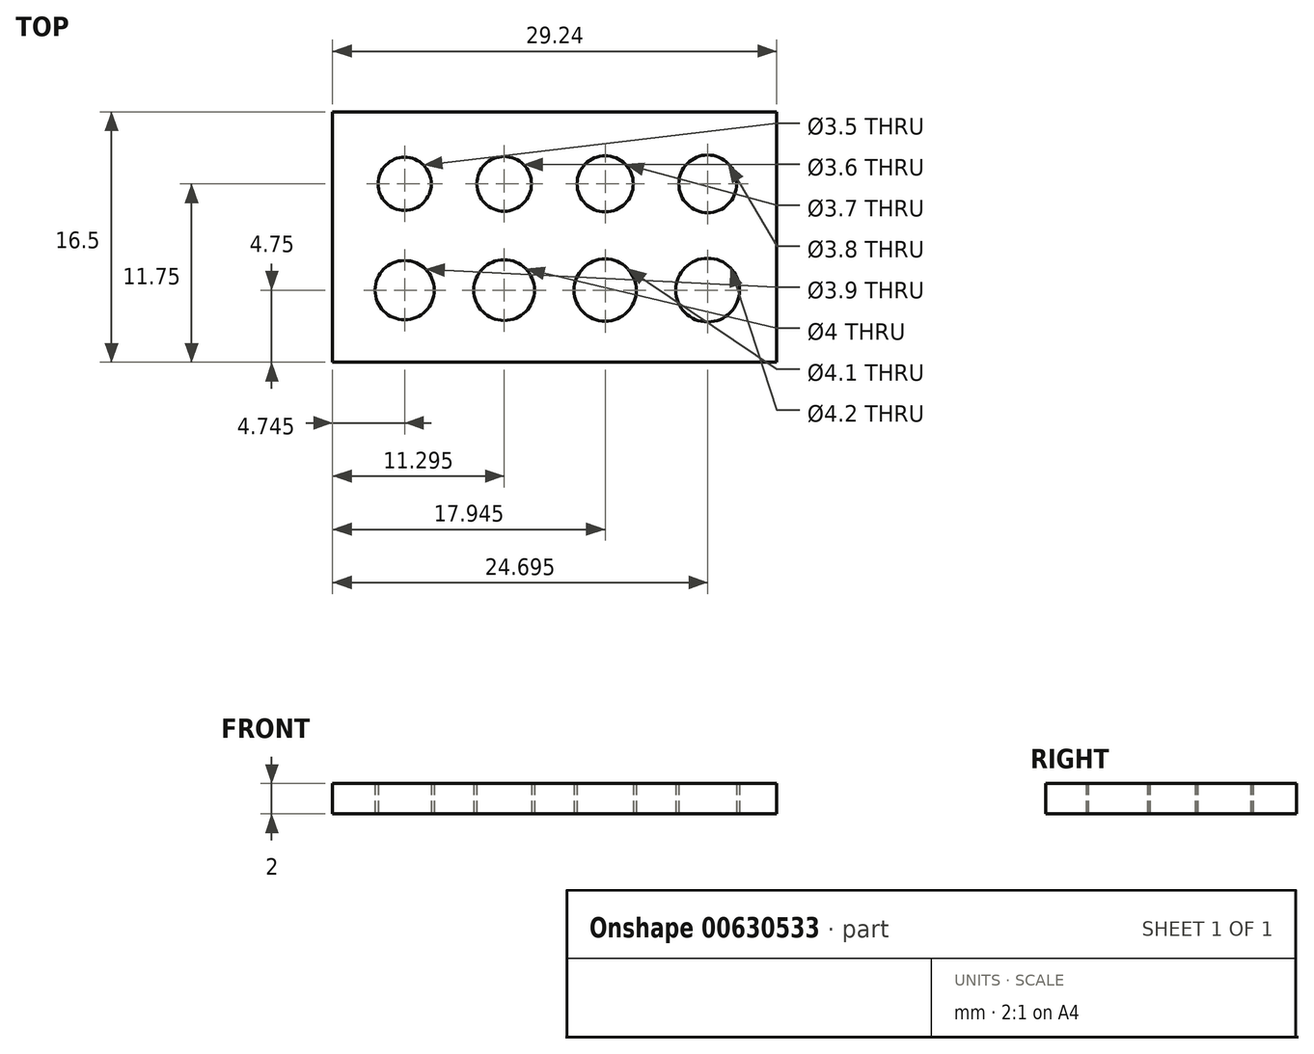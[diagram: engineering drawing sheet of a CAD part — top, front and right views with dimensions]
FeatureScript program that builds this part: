
annotation { "Feature Type Name" : "Feature", "Feature Type Description" : "" }
export const myFeature = defineFeature(function(context is Context, id is Id, definition is map)
    precondition{}
    {
        {
            var Q0;
            Q0=qCreatedBy(makeId("Top.planeOp"),FACE);
            var sketch = newSketch(context, id + "F0", { "sketchPlane" : qUnion([Q0])});
            skCircle(sketch, "E0", {"center": v(-9.88, 11.75) * mm, "radius": 1.75 * mm});
            skCircle(sketch, "E1", {"center": v(-3.32, 11.75) * mm, "radius": 1.8 * mm});
            skCircle(sketch, "E2", {"center": v(3.33, 11.75) * mm, "radius": 1.85 * mm});
            skCircle(sketch, "E3", {"center": v(10.08, 11.75) * mm, "radius": 1.9 * mm});
            skCircle(sketch, "E4", {"center": v(-9.88, 4.75) * mm, "radius": 1.95 * mm});
            skCircle(sketch, "E5", {"center": v(-3.33, 4.75) * mm, "radius": 2 * mm});
            skCircle(sketch, "E6", {"center": v(3.33, 4.75) * mm, "radius": 2.05 * mm});
            skCircle(sketch, "E7", {"center": v(10.08, 4.75) * mm, "radius": 2.1 * mm});
            skLineSegment(sketch, "E8", {"start": v(-3.32, 11.75) * mm, "end": v(3.33, 11.75) * mm, "construction": true});
            skLineSegment(sketch, "E9", {"start": v(3.32, 4.75) * mm, "end": v(3.32, 11.75) * mm, "construction": true});
            skLineSegment(sketch, "E10.bottom", {"start": v(-14.63, 16.5) * mm, "end": v(14.62, 16.5) * mm});
            skLineSegment(sketch, "E10.top", {"start": v(-14.63, 0) * mm, "end": v(14.62, 0) * mm});
            skLineSegment(sketch, "E10.left", {"start": v(-14.63, 16.5) * mm, "end": v(-14.63, 0) * mm});
            skLineSegment(sketch, "E10.right", {"start": v(14.62, 16.5) * mm, "end": v(14.62, 0) * mm});
            skPoint(sketch, "E10.middle", {"position": v(0, 8.25) * mm});
            skPoint(sketch, "E10.middle.positionSnap0", {"position": v(3.33, 8.25) * mm});
            skPoint(sketch, "E10.middle.positionSnap1", {"position": v(0, 11.75) * mm});
            skPoint(sketch, "E10.centerSnap0", {"position": v(3.33, 8.25) * mm});
            skPoint(sketch, "E10.centerSnap1", {"position": v(0, 11.75) * mm});
            skSolve(sketch);
        }
        {
            var Q0;
            Q0=makeQuery(id+"F0.imprint","IMPRINT",FACE,{"disambiguationData":[TD([[makeQuery(id+"F0.imprint","IMPRINT",EDGE,{"derivedFrom":sQuery(id+"F0.wireOp",EDGE,"E0")}),-1.0]])]});
            extrude(context, id + "F1", {"entities" : qUnion([Q0]), "depth" : 2 * mm, "offsetDistance" : 25 * mm});
        }
    });
